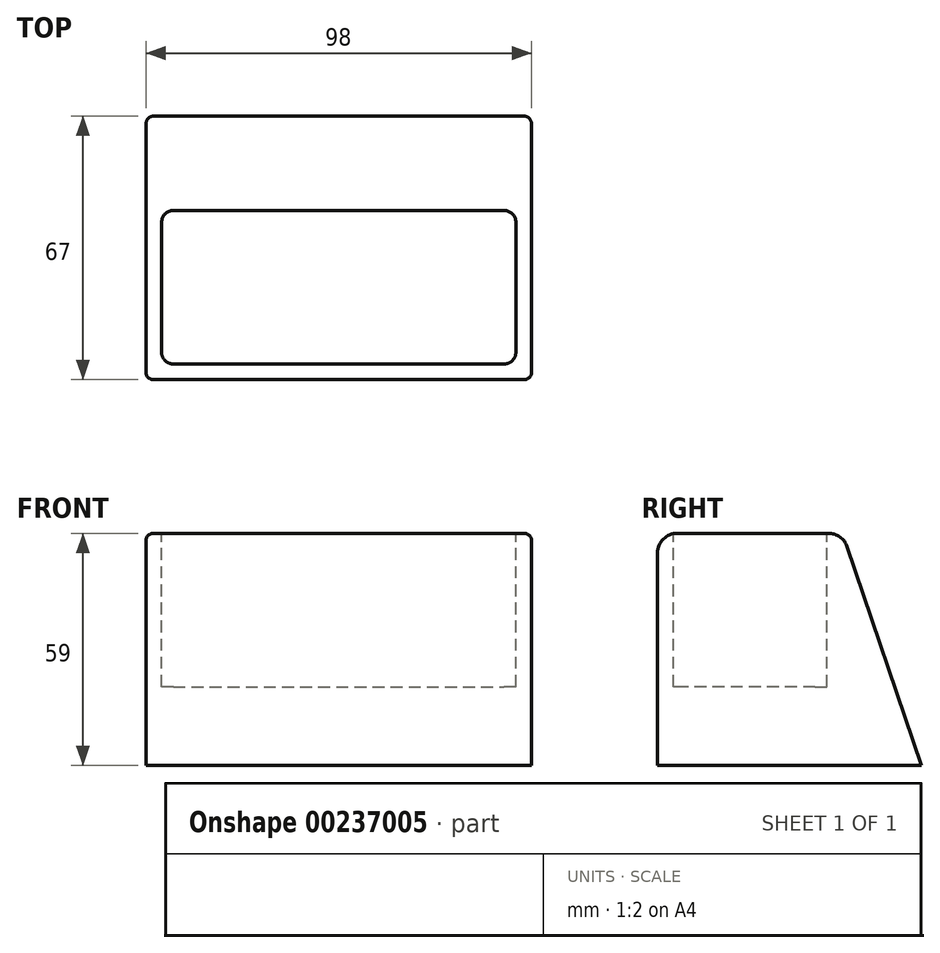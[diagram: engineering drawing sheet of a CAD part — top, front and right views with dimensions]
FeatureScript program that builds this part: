
annotation { "Feature Type Name" : "Feature", "Feature Type Description" : "" }
export const myFeature = defineFeature(function(context is Context, id is Id, definition is map)
    precondition{}
    {
        {
            var Q0;
            Q0=qCreatedBy(makeId("Right.planeOp"),FACE);
            var sketch = newSketch(context, id + "F0", { "sketchPlane" : qUnion([Q0])});
            skLineSegment(sketch, "E0", {"start": v(0, 0) * mm, "end": v(0, 59) * mm});
            skLineSegment(sketch, "E1", {"start": v(0, 59) * mm, "end": v(47, 59) * mm});
            skLineSegment(sketch, "E2", {"start": v(47, 59) * mm, "end": v(67, 0) * mm});
            skLineSegment(sketch, "E3", {"start": v(67, 0) * mm, "end": v(0, 0) * mm});
            skSolve(sketch);
        }
        {
            var Q0;
            Q0=makeQuery(id+"F0.imprint","IMPRINT",FACE,{"disambiguationData":[TD([[makeQuery(id+"F0.imprint","IMPRINT",EDGE,{"derivedFrom":sQuery(id+"F0.wireOp",EDGE,"E0")}),-1.0]])]});
            extrude(context, id + "F1", {"entities" : qUnion([Q0]), "depth" : 98 * mm});
        }
        {
            var Q0;
            Q0=makeQuery(id+"F1.opExtrude","SWEPT_FACE",FACE,{"disambiguationData":[OSD([sQuery(id+"F0.wireOp",EDGE,"E1")])]});
            var sketch = newSketch(context, id + "F2", { "sketchPlane" : qUnion([Q0])});
            skLineSegment(sketch, "E4.bottom", {"start": v(7, 43) * mm, "end": v(91, 43) * mm});
            skLineSegment(sketch, "E4.top", {"start": v(7, 4) * mm, "end": v(91, 4) * mm});
            skLineSegment(sketch, "E4.left", {"start": v(4, 40) * mm, "end": v(4, 7) * mm});
            skLineSegment(sketch, "E4.right", {"start": v(94, 40) * mm, "end": v(94, 7) * mm});
            skPoint(sketch, "E5.visualSharp", {"position": v(4, 43) * mm});
            skArc(sketch, "E5.filletArc", {"start": v(7, 43) * mm, "mid": v(4.88, 42.12) * mm, "end": v(4, 40) * mm});
            skPoint(sketch, "E6.visualSharp", {"position": v(94, 43) * mm});
            skArc(sketch, "E6.filletArc", {"start": v(94, 40) * mm, "mid": v(93.12, 42.12) * mm, "end": v(91, 43) * mm});
            skPoint(sketch, "E7.visualSharp", {"position": v(94, 4) * mm});
            skArc(sketch, "E7.filletArc", {"start": v(91, 4) * mm, "mid": v(93.12, 4.88) * mm, "end": v(94, 7) * mm});
            skPoint(sketch, "E8.visualSharp", {"position": v(4, 4) * mm});
            skArc(sketch, "E8.filletArc", {"start": v(4, 7) * mm, "mid": v(4.88, 4.88) * mm, "end": v(7, 4) * mm});
            skSolve(sketch);
        }
        {
            var Q0;
            Q0 = qSketchRegion(id + "F2", true);
            extrude(context, id + "F3", {"entities" : qUnion([Q0]), "operationType" : NewBodyOperationType.REMOVE, "oppositeDirection" : true, "depth" : 39 * mm});
        }
        {
            var Q0;
            Q0=makeQuery(id+"F1.opExtrude","SWEPT_EDGE",EDGE,{"disambiguationData":[OSD([sQuery(id+"F0.wireOp",EDGE,"E0"),sQuery(id+"F0.wireOp",EDGE,"E1")])]});
            var Q1;
            Q1=makeQuery(id+"F1.opExtrude","SWEPT_EDGE",EDGE,{"disambiguationData":[OSD([sQuery(id+"F0.wireOp",EDGE,"E1"),sQuery(id+"F0.wireOp",EDGE,"E2")])]});
            fillet(context, id + "F4", {"entities" : qUnion([Q0, Q1]), "radius" : 5 * mm, "tangentPropagation" : true, "allowEdgeOverflow" : false});
        }
        {
            var Q0;
            Q0=makeQuery(id+"F1.opExtrude","CAP_EDGE",EDGE,{"disambiguationData":[OSD([sQuery(id+"F0.wireOp",EDGE,"E1")])],"isStart":true});
            var Q1;
            Q1=makeQuery(id+"F1.opExtrude","CAP_EDGE",EDGE,{"disambiguationData":[OSD([sQuery(id+"F0.wireOp",EDGE,"E1")])],"isStart":false});
            fillet(context, id + "F5", {"entities" : qUnion([Q0, Q1]), "radius" : 2 * mm, "tangentPropagation" : true, "allowEdgeOverflow" : false});
        }
    });
